# Revit family: Domotics-DomesticRanges-GEWISS-SYSTEM_COMMAND-IR_MOVEMENT_DETECTOR
name_source: partatom
category: Apparecchi elettrici
revit_build: Autodesk Revit 2016 (Build: 20161004_0715(x64)
units: mm (PartAtom-declared; Revit-internal decimal feet)

## family parameters
Condiviso = Sì
Host = Superficie
Mantenere orientamento annotazione = Sì
Numero OmniClass = 23.80.50.11.14
Punto di calcolo locali = Sì
Quota connettore circolare = Usa diametro
Taglio con vuoti quando caricato = Sì
Tipo di parte = Normale
Titolo OmniClass = Switches

## types (2) — shared parameters
Carico apparente = 0 VA
Catalogue = DOMOTICS
Catalogue Range = SYSTEM - DOMESTIC RANGE
Description. = Movement detector
IDF = f974fdf7-cc1f-430c-8fe3-511b1c6b9308
IDT = f1536965-6def-473c-817a-fe496fe07dc3
Immagine tipo = GW21821.jpg
Larghezza = 23 mm  [stored 0.0754593 ft]
N. poli = 1
No. SYSTEM modules = 1
Produttore = GEWISS S.p.A.
Prospetto di default = 1219 mm
SEO = Detector
Simbolo = SIMBOLO RILEVATORI MOVIMENTO : IR
Supply voltage = 230V ac - 50/60Hz
Technical sheet = https://www.gewiss.com
Technology = IR light switch
Tipo_ = SYSTEM INFRARED_BASE : GW21821 - Nero - Rivelatore di movimento
Type = IR light switch
URL = https://www.gewiss.com
Version file RFA = 19.4
Volt = 230 V
Voltage = 230V ac - 50/60 Hz

## per-type parameters (varying)
| type | Colour | Descrizione | EAN code | Electrocod | Modello |
| GW21821 - 230V 50hz pass.infra-red detector black | Black | 230V 50HZ PASS.INFRA-RED DETECTOR SY/BK | 8011564128293 | 0531 | GW21821 |
| GW20821 - 230V 50hz pass.infra-red detector white | White | 230V 50HZ PASS.INFRA-RED DETECTOR SY/WT | 8011564038561 | 0513 | GW20821 |

note: [stored X ft] marks values corroborated as IEEE doubles in the binary element streams (Revit-internal decimal feet)

## geometry (parser evidence)
native form markers: Sweep x2
no freeform markers — native parametric forms only
